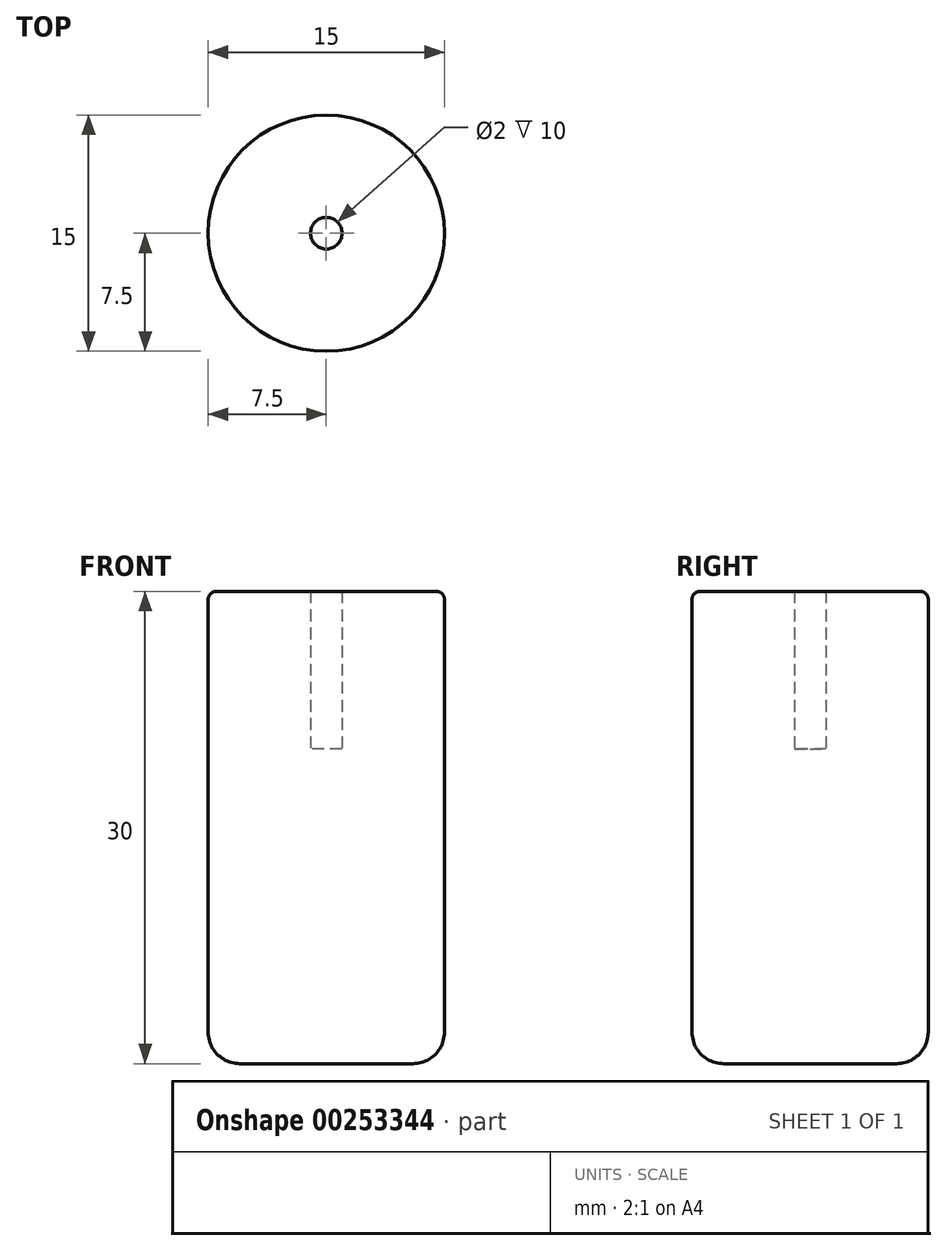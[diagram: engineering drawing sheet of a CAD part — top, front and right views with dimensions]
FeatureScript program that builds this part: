
annotation { "Feature Type Name" : "Feature", "Feature Type Description" : "" }
export const myFeature = defineFeature(function(context is Context, id is Id, definition is map)
    precondition{}
    {
        {
            var Q0;
            Q0=qCreatedBy(makeId("Top.planeOp"),FACE);
            var sketch = newSketch(context, id + "F0", { "sketchPlane" : qUnion([Q0])});
            skCircle(sketch, "E0", {"center": v(0, 0) * mm, "radius": 7.5 * mm});
            skCircle(sketch, "E1", {"center": v(0, 0) * mm, "radius": 1 * mm});
            skSolve(sketch);
        }
        {
            var Q0;
            Q0=makeQuery(id+"F0.imprint","IMPRINT",FACE,{"disambiguationData":[TD([[makeQuery(id+"F0.imprint","IMPRINT",EDGE,{"derivedFrom":sQuery(id+"F0.wireOp",EDGE,"E0")}),1.0]])]});
            extrude(context, id + "F1", {"entities" : qUnion([Q0]), "depth" : 30 * mm});
        }
        {
            var Q0;
            Q0=makeQuery(id+"F0.imprint","IMPRINT",FACE,{"disambiguationData":[TD([[makeQuery(id+"F0.imprint","IMPRINT",EDGE,{"derivedFrom":sQuery(id+"F0.wireOp",EDGE,"E1")}),1.0]])]});
            extrude(context, id + "F2", {"entities" : qUnion([Q0]), "operationType" : NewBodyOperationType.ADD, "depth" : 20 * mm});
        }
        {
            var Q0;
            Q0=makeQuery(id+"F1.opExtrude","CAP_EDGE",EDGE,{"disambiguationData":[OSD([sQuery(id+"F0.wireOp",EDGE,"E0")])],"isStart":true});
            fillet(context, id + "F3", {"entities" : qUnion([Q0]), "radius" : 2 * mm, "tangentPropagation" : true, "allowEdgeOverflow" : false});
        }
        {
            var Q0;
            Q0=makeQuery(id+"F1.opExtrude","CAP_EDGE",EDGE,{"disambiguationData":[OSD([sQuery(id+"F0.wireOp",EDGE,"E0")])],"isStart":false});
            fillet(context, id + "F4", {"entities" : qUnion([Q0]), "radius" : 0.5 * mm, "tangentPropagation" : true, "allowEdgeOverflow" : false});
        }
    });
